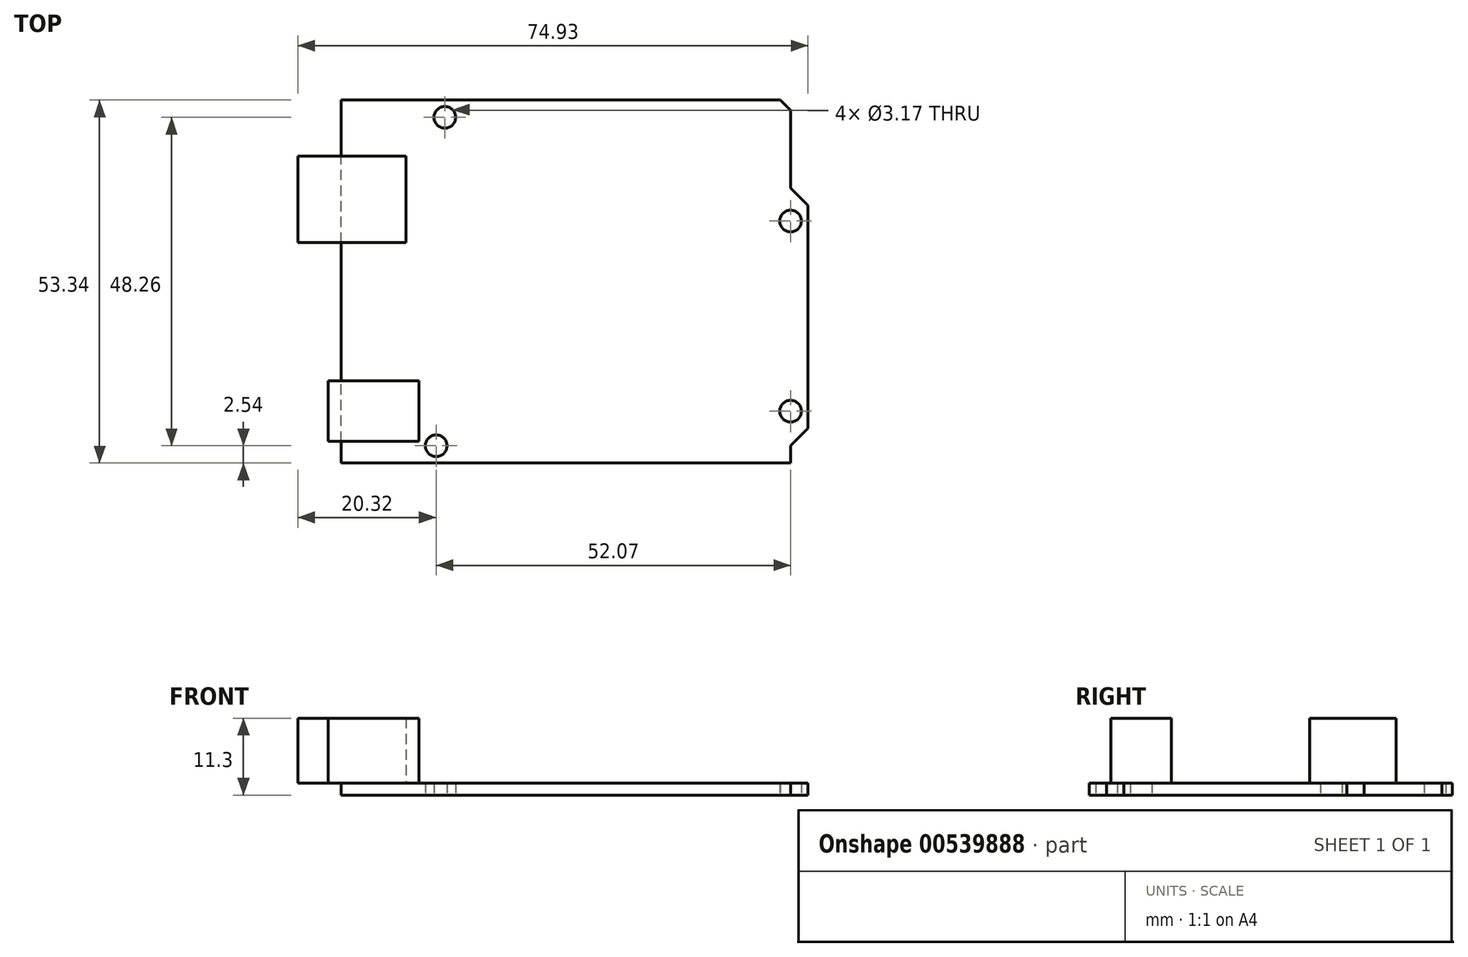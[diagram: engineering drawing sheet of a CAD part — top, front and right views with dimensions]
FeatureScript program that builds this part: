
annotation { "Feature Type Name" : "Feature", "Feature Type Description" : "" }
export const myFeature = defineFeature(function(context is Context, id is Id, definition is map)
    precondition{}
    {
        {
            var Q0;
            Q0=qCreatedBy(makeId("Top.planeOp"),FACE);
            var sketch = newSketch(context, id + "F0", { "sketchPlane" : qUnion([Q0])});
            skLineSegment(sketch, "E0", {"start": v(13.97, 0) * mm, "end": v(66.04, 0) * mm});
            skLineSegment(sketch, "E1", {"start": v(0, 0) * mm, "end": v(0, 53.34) * mm});
            skLineSegment(sketch, "E2", {"start": v(0, 53.34) * mm, "end": v(64.52, 53.34) * mm});
            skLineSegment(sketch, "E3", {"start": v(66.04, 0) * mm, "end": v(66.04, 2.54) * mm});
            skLineSegment(sketch, "E4", {"start": v(66.04, 51.82) * mm, "end": v(64.52, 53.34) * mm});
            skLineSegment(sketch, "E5", {"start": v(68.58, 5.08) * mm, "end": v(68.58, 37.85) * mm});
            skLineSegment(sketch, "E6", {"start": v(68.58, 5.08) * mm, "end": v(66.04, 2.54) * mm});
            skPoint(sketch, "E7", {"position": v(66.04, 40.39) * mm});
            skLineSegment(sketch, "E8", {"start": v(66.04, 40.39) * mm, "end": v(68.58, 37.85) * mm});
            skLineSegment(sketch, "E9.trimOffspring", {"start": v(66.04, 40.39) * mm, "end": v(66.04, 51.82) * mm});
            skCircle(sketch, "E10", {"center": v(66.04, 7.62) * mm, "radius": 1.59 * mm});
            skPoint(sketch, "E10.centerSnap0", {"position": v(66.04, 1.27) * mm});
            skCircle(sketch, "E11", {"center": v(66.04, 35.56) * mm, "radius": 1.59 * mm});
            skLineSegment(sketch, "E12", {"start": v(13.97, 0) * mm, "end": v(15.24, 0) * mm});
            skCircle(sketch, "E13", {"center": v(15.24, 50.8) * mm, "radius": 1.59 * mm});
            skLineSegment(sketch, "E14", {"start": v(0, 0) * mm, "end": v(13.97, 0) * mm});
            skCircle(sketch, "E15", {"center": v(13.97, 2.54) * mm, "radius": 1.59 * mm});
            skLineSegment(sketch, "E16", {"start": v(0, 0) * mm, "end": v(0, 32.39) * mm});
            skPoint(sketch, "E17.end.orphan", {"position": v(9.53, 43.82) * mm});
            skPoint(sketch, "E18.end.orphan", {"position": v(9.53, 32.39) * mm});
            skSolve(sketch);
        }
        {
            var Q0;
            Q0 = qSketchRegion(id + "F0", true);
            extrude(context, id + "F1", {"entities" : qUnion([Q0]), "depth" : 1.78 * mm, "offsetDistance" : 25.4 * mm});
        }
        {
            var Q0;
            Q0=makeQuery(id+"F1.opExtrude","CAP_FACE",FACE,{"disambiguationData":[OSD([sQuery(id+"F0.wireOp",EDGE,"E0"),sQuery(id+"F0.wireOp",EDGE,"E1"),sQuery(id+"F0.wireOp",EDGE,"E2"),sQuery(id+"F0.wireOp",EDGE,"E4"),sQuery(id+"F0.wireOp",EDGE,"E3"),sQuery(id+"F0.wireOp",EDGE,"E5"),sQuery(id+"F0.wireOp",EDGE,"E6"),sQuery(id+"F0.wireOp",EDGE,"E8"),sQuery(id+"F0.wireOp",EDGE,"E9.trimOffspring"),sQuery(id+"F0.wireOp",EDGE,"E10"),sQuery(id+"F0.wireOp",EDGE,"E11"),sQuery(id+"F0.wireOp",EDGE,"E12"),sQuery(id+"F0.wireOp",EDGE,"E13"),sQuery(id+"F0.wireOp",EDGE,"E14"),sQuery(id+"F0.wireOp",EDGE,"E15"),sQuery(id+"F0.wireOp",EDGE,"E16")])],"isStart":false});
            var sketch = newSketch(context, id + "F2", { "sketchPlane" : qUnion([Q0])});
            skLineSegment(sketch, "E19", {"start": v(0, 0) * mm, "end": v(0, 32.39) * mm});
            skLineSegment(sketch, "E20", {"start": v(9.52, 32.39) * mm, "end": v(9.52, 45.09) * mm});
            skLineSegment(sketch, "E21", {"start": v(-6.35, 45.09) * mm, "end": v(-6.35, 32.39) * mm});
            skLineSegment(sketch, "E22", {"start": v(0, 0) * mm, "end": v(0, 3.18) * mm});
            skLineSegment(sketch, "E23", {"start": v(11.43, 3.18) * mm, "end": v(11.43, 12.07) * mm});
            skLineSegment(sketch, "E24", {"start": v(11.43, 12.07) * mm, "end": v(-1.9, 12.07) * mm});
            skLineSegment(sketch, "E25", {"start": v(-1.9, 12.07) * mm, "end": v(-1.9, 3.18) * mm});
            skLineSegment(sketch, "E26", {"start": v(-1.9, 3.18) * mm, "end": v(11.43, 3.18) * mm});
            skLineSegment(sketch, "E27", {"start": v(-6.35, 32.39) * mm, "end": v(9.52, 32.39) * mm});
            skLineSegment(sketch, "E28", {"start": v(9.52, 45.09) * mm, "end": v(-6.35, 45.09) * mm});
            skSolve(sketch);
        }
        {
            var Q0;
            Q0 = qSketchRegion(id + "F2", true);
            extrude(context, id + "F3", {"entities" : qUnion([Q0]), "operationType" : NewBodyOperationType.ADD, "depth" : 9.52 * mm, "offsetDistance" : 25.4 * mm});
        }
    });
